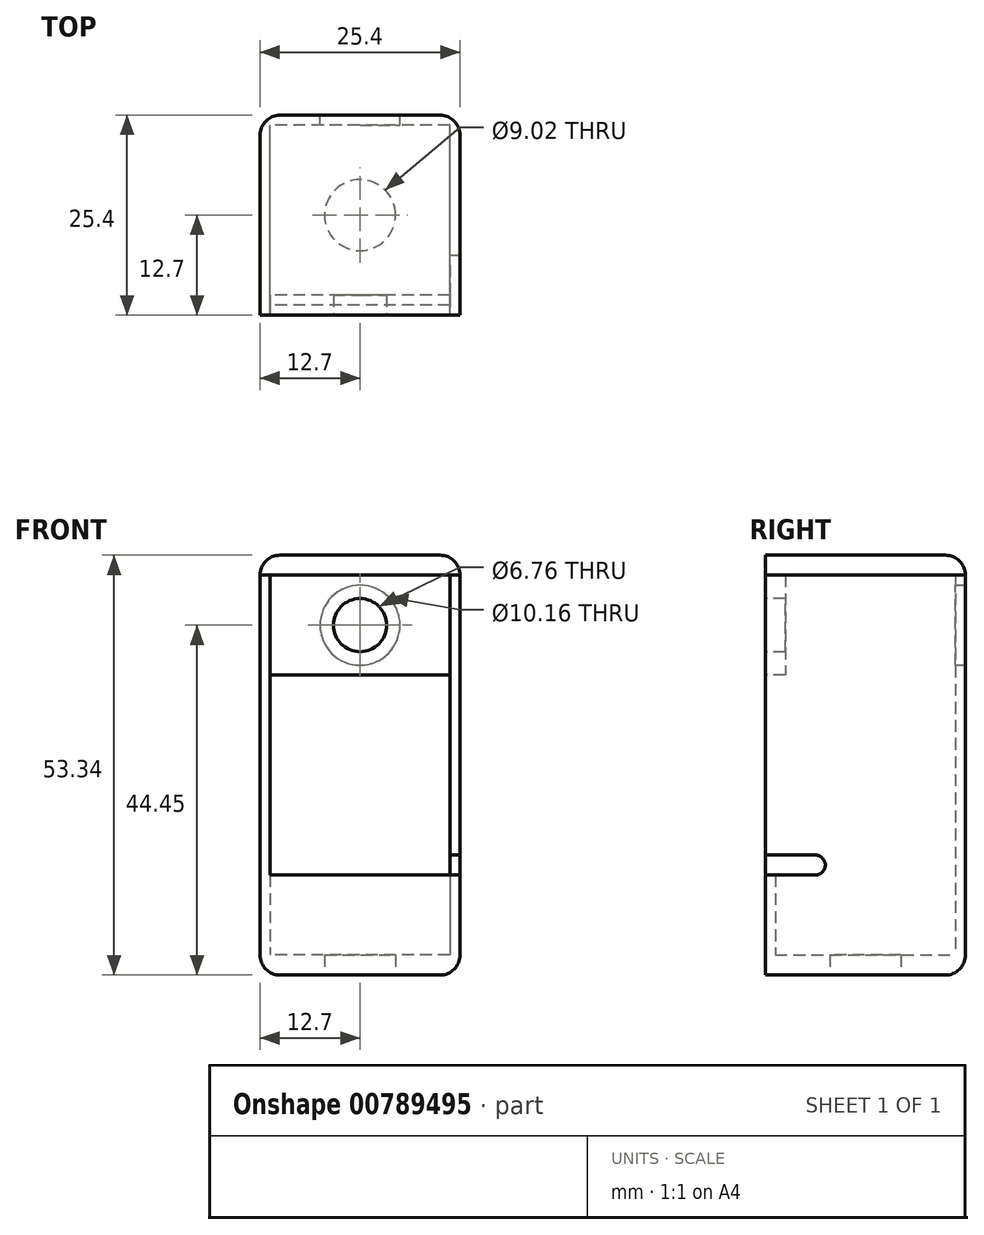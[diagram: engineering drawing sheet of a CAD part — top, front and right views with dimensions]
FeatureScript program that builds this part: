
annotation { "Feature Type Name" : "Feature", "Feature Type Description" : "" }
export const myFeature = defineFeature(function(context is Context, id is Id, definition is map)
    precondition{}
    {
        {
            var Q0;
            Q0=qCreatedBy(makeId("Top.planeOp"),FACE);
            var sketch = newSketch(context, id + "F0", { "sketchPlane" : qUnion([Q0])});
            skLineSegment(sketch, "E0.bottom", {"start": v(12.7, -12.7) * mm, "end": v(-12.7, -12.7) * mm});
            skLineSegment(sketch, "E0.top", {"start": v(12.7, 12.7) * mm, "end": v(-12.7, 12.7) * mm});
            skLineSegment(sketch, "E0.left", {"start": v(12.7, -12.7) * mm, "end": v(12.7, 12.7) * mm});
            skLineSegment(sketch, "E0.right", {"start": v(-12.7, -12.7) * mm, "end": v(-12.7, 12.7) * mm});
            skPoint(sketch, "E0.middle", {"position": v(0, 0) * mm});
            skLineSegment(sketch, "E1.bottom", {"start": v(11.43, -11.43) * mm, "end": v(-11.43, -11.43) * mm});
            skLineSegment(sketch, "E1.top", {"start": v(11.43, 11.43) * mm, "end": v(-11.43, 11.43) * mm});
            skLineSegment(sketch, "E1.left", {"start": v(11.43, -11.43) * mm, "end": v(11.43, 11.43) * mm});
            skLineSegment(sketch, "E1.right", {"start": v(-11.43, -11.43) * mm, "end": v(-11.43, 11.43) * mm});
            skSolve(sketch);
        }
        {
            var Q0;
            Q0 = qSketchRegion(id + "F0", true);
            extrude(context, id + "F1", {"entities" : qUnion([Q0]), "depth" : 50.8 * mm, "offsetDistance" : 25.4 * mm});
        }
        {
            var Q0;
            Q0=makeQuery(id+"F1.opExtrude","CAP_FACE",FACE,{"disambiguationData":[OSD([sQuery(id+"F0.wireOp",EDGE,"E0.bottom"),sQuery(id+"F0.wireOp",EDGE,"E0.top"),sQuery(id+"F0.wireOp",EDGE,"E0.left"),sQuery(id+"F0.wireOp",EDGE,"E0.right"),sQuery(id+"F0.wireOp",EDGE,"E1.bottom"),sQuery(id+"F0.wireOp",EDGE,"E1.top"),sQuery(id+"F0.wireOp",EDGE,"E1.left"),sQuery(id+"F0.wireOp",EDGE,"E1.right")])],"isStart":true});
            var sketch = newSketch(context, id + "F2", { "sketchPlane" : qUnion([Q0])});
            skCircle(sketch, "E2", {"center": v(0, 0) * mm, "radius": 4.5 * mm});
            skLineSegment(sketch, "E3.bottom", {"start": v(-11.43, 11.43) * mm, "end": v(11.43, 11.43) * mm});
            skLineSegment(sketch, "E3.top", {"start": v(-11.43, -11.43) * mm, "end": v(11.43, -11.43) * mm});
            skLineSegment(sketch, "E3.left", {"start": v(-11.43, 11.43) * mm, "end": v(-11.43, -11.43) * mm});
            skLineSegment(sketch, "E3.right", {"start": v(11.43, 11.43) * mm, "end": v(11.43, -11.43) * mm});
            skSolve(sketch);
        }
        {
            var Q0;
            Q0 = qSketchRegion(id + "F2", true);
            extrude(context, id + "F3", {"entities" : qUnion([Q0]), "operationType" : NewBodyOperationType.ADD, "oppositeDirection" : true, "depth" : 2.54 * mm, "offsetDistance" : 25.4 * mm});
        }
        {
            var Q0;
            Q0=makeQuery(id+"F1.opExtrude","CAP_FACE",FACE,{"disambiguationData":[OSD([sQuery(id+"F0.wireOp",EDGE,"E0.bottom"),sQuery(id+"F0.wireOp",EDGE,"E0.top"),sQuery(id+"F0.wireOp",EDGE,"E0.left"),sQuery(id+"F0.wireOp",EDGE,"E0.right"),sQuery(id+"F0.wireOp",EDGE,"E1.bottom"),sQuery(id+"F0.wireOp",EDGE,"E1.top"),sQuery(id+"F0.wireOp",EDGE,"E1.left"),sQuery(id+"F0.wireOp",EDGE,"E1.right")])],"isStart":false});
            var sketch = newSketch(context, id + "F4", { "sketchPlane" : qUnion([Q0])});
            skLineSegment(sketch, "E4.bottom", {"start": v(-11.43, -11.43) * mm, "end": v(11.43, -11.43) * mm});
            skLineSegment(sketch, "E4.top", {"start": v(-11.43, -12.7) * mm, "end": v(11.43, -12.7) * mm});
            skLineSegment(sketch, "E4.left", {"start": v(-11.43, -11.43) * mm, "end": v(-11.43, -12.7) * mm});
            skLineSegment(sketch, "E4.right", {"start": v(11.43, -11.43) * mm, "end": v(11.43, -12.7) * mm});
            skSolve(sketch);
        }
        {
            var Q0;
            Q0 = qSketchRegion(id + "F4", true);
            extrude(context, id + "F5", {"entities" : qUnion([Q0]), "operationType" : NewBodyOperationType.REMOVE, "oppositeDirection" : true, "depth" : 38.1 * mm, "offsetDistance" : 25.4 * mm});
        }
        {
            var Q0;
            Q0=makeQuery(id+"F1.opExtrude","SWEPT_FACE",FACE,{"disambiguationData":[OSD([sQuery(id+"F0.wireOp",EDGE,"E0.left")])]});
            var sketch = newSketch(context, id + "F6", { "sketchPlane" : qUnion([Q0])});
            skArc(sketch, "E5", {"start": v(-6.35, 12.7) * mm, "mid": v(-5.08, 13.97) * mm, "end": v(-6.35, 15.24) * mm});
            skLineSegment(sketch, "E6", {"start": v(-6.35, 15.24) * mm, "end": v(-12.7, 15.24) * mm});
            skLineSegment(sketch, "E7", {"start": v(-12.7, 15.24) * mm, "end": v(-12.7, 12.7) * mm});
            skLineSegment(sketch, "E8", {"start": v(-12.7, 12.7) * mm, "end": v(-6.35, 12.7) * mm});
            skSolve(sketch);
        }
        {
            var Q0;
            Q0 = qSketchRegion(id + "F6", true);
            extrude(context, id + "F7", {"entities" : qUnion([Q0]), "operationType" : NewBodyOperationType.REMOVE, "oppositeDirection" : true, "depth" : 2.54 * mm, "offsetDistance" : 25.4 * mm});
        }
        {
            var Q0;
            Q0=makeQuery(id+"F1.opExtrude","SWEPT_FACE",FACE,{"disambiguationData":[OSD([sQuery(id+"F0.wireOp",EDGE,"E0.bottom")])]});
            var sketch = newSketch(context, id + "F8", { "sketchPlane" : qUnion([Q0])});
            skLineSegment(sketch, "E9.bottom", {"start": v(11.43, 50.8) * mm, "end": v(-11.43, 50.8) * mm});
            skLineSegment(sketch, "E9.top", {"start": v(11.43, 38.1) * mm, "end": v(-11.43, 38.1) * mm});
            skLineSegment(sketch, "E9.left", {"start": v(11.43, 50.8) * mm, "end": v(11.43, 38.1) * mm});
            skLineSegment(sketch, "E9.right", {"start": v(-11.43, 50.8) * mm, "end": v(-11.43, 38.1) * mm});
            skSolve(sketch);
        }
        {
            var Q0;
            Q0 = qSketchRegion(id + "F8", true);
            extrude(context, id + "F9", {"entities" : qUnion([Q0]), "oppositeDirection" : true, "depth" : 2.54 * mm, "offsetDistance" : 25.4 * mm});
        }
        {
            var Q0;
            Q0=makeQuery(id+"F9.opExtrude","CAP_FACE",FACE,{"disambiguationData":[OSD([sQuery(id+"F8.wireOp",EDGE,"E9.bottom"),sQuery(id+"F8.wireOp",EDGE,"E9.top"),sQuery(id+"F8.wireOp",EDGE,"E9.left"),sQuery(id+"F8.wireOp",EDGE,"E9.right")])],"isStart":true});
            var sketch = newSketch(context, id + "F10", { "sketchPlane" : qUnion([Q0])});
            skLineSegment(sketch, "E10", {"start": v(0, 38.1) * mm, "end": v(0, 50.8) * mm, "construction": true});
            skPoint(sketch, "E11", {"position": v(0, 44.45) * mm});
            skSolve(sketch);
        }
        {
            var Q0;
            Q0=sQuery(id+"F10.wireOp",VERTEX,"E11");
            var Q1;
            Q1=makeQuery(id+"F1.opExtrude","SWEPT_BODY",BODY,{"disambiguationData":[OSD([sQuery(id+"F0.wireOp",EDGE,"E0.bottom"),sQuery(id+"F0.wireOp",EDGE,"E0.top"),sQuery(id+"F0.wireOp",EDGE,"E0.left"),sQuery(id+"F0.wireOp",EDGE,"E0.right"),sQuery(id+"F0.wireOp",EDGE,"E1.bottom"),sQuery(id+"F0.wireOp",EDGE,"E1.top"),sQuery(id+"F0.wireOp",EDGE,"E1.left"),sQuery(id+"F0.wireOp",EDGE,"E1.right")])]});
            var Q2;
            Q2=makeQuery(id+"F9.opExtrude","SWEPT_BODY",BODY,{"disambiguationData":[OSD([sQuery(id+"F8.wireOp",EDGE,"E9.bottom"),sQuery(id+"F8.wireOp",EDGE,"E9.top"),sQuery(id+"F8.wireOp",EDGE,"E9.left"),sQuery(id+"F8.wireOp",EDGE,"E9.right")])]});
            hole(context, id + "F11", {"style" : HoleStyle.SIMPLE, "endStyle" : HoleEndStyle.THROUGH, "standardTappedOrClearance" : lookupTablePath({ "standard" : "ANSI", "fit" : "Normal (ASME)", "size" : "1/4", "type" : "Clearance" }), "standardBlindInLast" : lookupTablePath({ "fit" : "Free", "standard" : "ANSI", "size" : "1/4", "type" : "Clearance" }), "holeDiameter" : 6.76 * mm, "majorDiameter" : 6.35 * mm, "isTappedThrough" : true, "tappedDepth" : 12.7 * mm, "tapClearance" : 3, "startFromSketch" : true, "locations" : qUnion([Q0]), "scope" : qUnion([Q1, Q2])});
        }
        {
            var Q0;
            Q0=makeQuery(id+"F1.opExtrude","SWEPT_FACE",FACE,{"disambiguationData":[OSD([sQuery(id+"F0.wireOp",EDGE,"E0.top")])]});
            var sketch = newSketch(context, id + "F12", { "sketchPlane" : qUnion([Q0])});
            skCircle(sketch, "E12", {"center": v(0, 44.45) * mm, "radius": 5.08 * mm});
            skSolve(sketch);
        }
        {
            var Q0;
            Q0 = qSketchRegion(id + "F12", true);
            var Q1;
            Q1=makeQuery(id+"F1.opExtrude","SWEPT_FACE",FACE,{"disambiguationData":[OSD([sQuery(id+"F0.wireOp",EDGE,"E1.top")])]});
            extrude(context, id + "F13", {"entities" : qUnion([Q0]), "operationType" : NewBodyOperationType.REMOVE, "endBound" : BoundingType.UP_TO_SURFACE, "oppositeDirection" : true, "depth" : 25.4 * mm, "endBoundEntityFace" : qUnion([Q1]), "offsetDistance" : 25.4 * mm});
        }
        {
            var Q0;
            Q0=makeQuery(id+"F1.opExtrude","CAP_FACE",FACE,{"disambiguationData":[OSD([sQuery(id+"F0.wireOp",EDGE,"E0.bottom"),sQuery(id+"F0.wireOp",EDGE,"E0.top"),sQuery(id+"F0.wireOp",EDGE,"E0.left"),sQuery(id+"F0.wireOp",EDGE,"E0.right"),sQuery(id+"F0.wireOp",EDGE,"E1.bottom"),sQuery(id+"F0.wireOp",EDGE,"E1.top"),sQuery(id+"F0.wireOp",EDGE,"E1.left"),sQuery(id+"F0.wireOp",EDGE,"E1.right")])],"isStart":false});
            var sketch = newSketch(context, id + "F14", { "sketchPlane" : qUnion([Q0])});
            skLineSegment(sketch, "E13.bottom", {"start": v(12.7, 12.7) * mm, "end": v(-12.7, 12.7) * mm});
            skLineSegment(sketch, "E13.top", {"start": v(12.7, -12.7) * mm, "end": v(-12.7, -12.7) * mm});
            skLineSegment(sketch, "E13.left", {"start": v(12.7, 12.7) * mm, "end": v(12.7, -12.7) * mm});
            skLineSegment(sketch, "E13.right", {"start": v(-12.7, 12.7) * mm, "end": v(-12.7, -12.7) * mm});
            skSolve(sketch);
        }
        {
            var Q0;
            Q0 = qSketchRegion(id + "F14", true);
            extrude(context, id + "F15", {"entities" : qUnion([Q0]), "depth" : 2.54 * mm, "offsetDistance" : 25.4 * mm});
        }
        {
            var Q0;
            Q0=makeQuery(id+"F1.opExtrude","SWEPT_EDGE",EDGE,{"disambiguationData":[OSD([sQuery(id+"F0.wireOp",EDGE,"E0.top"),sQuery(id+"F0.wireOp",EDGE,"E0.left")])]});
            var Q1;
            Q1=makeQuery(id+"F15.opExtrude","SWEPT_EDGE",EDGE,{"disambiguationData":[OSD([sQuery(id+"F14.wireOp",EDGE,"E13.bottom"),sQuery(id+"F14.wireOp",EDGE,"E13.left")])]});
            var Q2;
            Q2=makeQuery(id+"F1.opExtrude","SWEPT_EDGE",EDGE,{"disambiguationData":[OSD([sQuery(id+"F0.wireOp",EDGE,"E0.top"),sQuery(id+"F0.wireOp",EDGE,"E0.right")])]});
            var Q3;
            Q3=makeQuery(id+"F15.opExtrude","SWEPT_EDGE",EDGE,{"disambiguationData":[OSD([sQuery(id+"F14.wireOp",EDGE,"E13.bottom"),sQuery(id+"F14.wireOp",EDGE,"E13.right")])]});
            var Q4;
            Q4=makeQuery(id+"F15.opExtrude","CAP_EDGE",EDGE,{"disambiguationData":[OSD([sQuery(id+"F14.wireOp",EDGE,"E13.bottom")])],"isStart":false});
            var Q5;
            Q5=makeQuery(id+"F15.opExtrude","CAP_EDGE",EDGE,{"disambiguationData":[OSD([sQuery(id+"F14.wireOp",EDGE,"E13.left")])],"isStart":false});
            var Q6;
            Q6=makeQuery(id+"F5.boolean.opBoolean","COPY",EDGE,{"derivedFrom":makeQuery(id+"F5.opExtrude","SWEPT_EDGE",EDGE,{"disambiguationData":[OSD([sQuery(id+"F0.wireOp",EDGE,"E0.bottom"),sQuery(id+"F4.wireOp",EDGE,"E4.top"),sQuery(id+"F4.wireOp",EDGE,"E4.left")])]})});
            var Q7;
            Q7=makeQuery(id+"F1.opExtrude","CAP_EDGE",EDGE,{"disambiguationData":[OSD([sQuery(id+"F0.wireOp",EDGE,"E0.top")])],"isStart":true});
            var Q8;
            Q8=makeQuery(id+"F1.opExtrude","CAP_EDGE",EDGE,{"disambiguationData":[OSD([sQuery(id+"F0.wireOp",EDGE,"E0.left")])],"isStart":true});
            var Q9;
            Q9=makeQuery(id+"F1.opExtrude","CAP_EDGE",EDGE,{"disambiguationData":[OSD([sQuery(id+"F0.wireOp",EDGE,"E0.right")])],"isStart":true});
            var Q10;
            Q10=makeQuery(id+"F15.opExtrude","CAP_EDGE",EDGE,{"disambiguationData":[OSD([sQuery(id+"F14.wireOp",EDGE,"E13.right")])],"isStart":false});
            fillet(context, id + "F16", {"entities" : qUnion([Q0, Q1, Q2, Q3, Q4, Q5, Q6, Q7, Q8, Q9, Q10]), "radius" : 2.54 * mm, "tangentPropagation" : true, "allowEdgeOverflow" : false});
        }
    });
